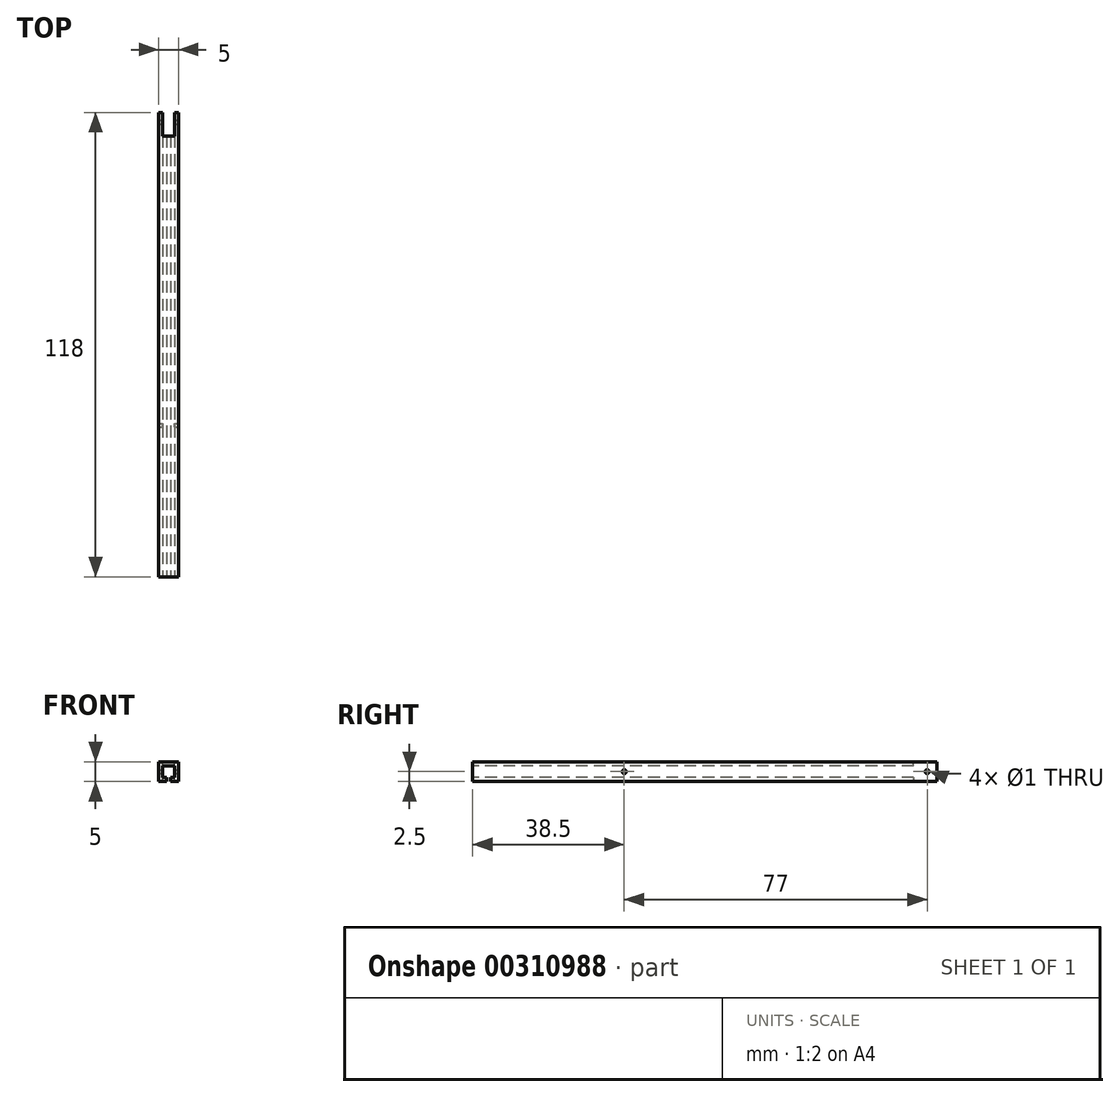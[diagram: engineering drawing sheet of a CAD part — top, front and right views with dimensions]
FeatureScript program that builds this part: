
annotation { "Feature Type Name" : "Feature", "Feature Type Description" : "" }
export const myFeature = defineFeature(function(context is Context, id is Id, definition is map)
    precondition{}
    {
        {
            var Q0;
            Q0=qCreatedBy(makeId("Front.planeOp"),FACE);
            var sketch = newSketch(context, id + "F0", { "sketchPlane" : qUnion([Q0])});
            skLineSegment(sketch, "E0.bottom", {"start": v(2.5, -2.5) * mm, "end": v(-2.5, -2.5) * mm});
            skLineSegment(sketch, "E0.top", {"start": v(2.5, 2.5) * mm, "end": v(-2.5, 2.5) * mm});
            skLineSegment(sketch, "E0.left", {"start": v(2.5, -2.5) * mm, "end": v(2.5, 2.5) * mm});
            skLineSegment(sketch, "E0.right", {"start": v(-2.5, -2.5) * mm, "end": v(-2.5, 2.5) * mm});
            skPoint(sketch, "E0.middle", {"position": v(0, 0) * mm});
            skSolve(sketch);
        }
        {
            var Q0;
            Q0=makeQuery(id+"F0.imprint","IMPRINT",FACE,{"disambiguationData":[TD([[makeQuery(id+"F0.imprint","IMPRINT",EDGE,{"derivedFrom":sQuery(id+"F0.wireOp",EDGE,"E0.bottom")}),-1.0]])]});
            extrude(context, id + "F1", {"entities" : qUnion([Q0]), "depth" : 118 * mm});
        }
        {
            var Q0;
            Q0=makeQuery(id+"F1.opExtrude","CAP_FACE",FACE,{"disambiguationData":[OSD([sQuery(id+"F0.wireOp",EDGE,"E0.bottom"),sQuery(id+"F0.wireOp",EDGE,"E0.top"),sQuery(id+"F0.wireOp",EDGE,"E0.left"),sQuery(id+"F0.wireOp",EDGE,"E0.right")])],"isStart":false});
            var sketch = newSketch(context, id + "F2", { "sketchPlane" : qUnion([Q0])});
            skLineSegment(sketch, "E1.bottom", {"start": v(1.5, -1.5) * mm, "end": v(-1.5, -1.5) * mm});
            skLineSegment(sketch, "E1.top", {"start": v(1.5, 1.5) * mm, "end": v(-1.5, 1.5) * mm});
            skLineSegment(sketch, "E1.left", {"start": v(1.5, -1.5) * mm, "end": v(1.5, 1.5) * mm});
            skLineSegment(sketch, "E1.right", {"start": v(-1.5, -1.5) * mm, "end": v(-1.5, 1.5) * mm});
            skPoint(sketch, "E1.middle", {"position": v(0, 0) * mm});
            skLineSegment(sketch, "E2", {"start": v(-0.5, -1.5) * mm, "end": v(-0.5, -2.5) * mm});
            skLineSegment(sketch, "E3", {"start": v(0.5, -1.5) * mm, "end": v(0.5, -2.5) * mm});
            skSolve(sketch);
        }
        {
            var Q0;
            Q0=makeQuery(id+"F2.imprint","IMPRINT",FACE,{"disambiguationData":[TD([[makeQuery(id+"F2.imprint","IMPRINT",EDGE,{"derivedFrom":sQuery(id+"F2.wireOp",EDGE,"E1.top")}),1.0]])]});
            var Q1;
            {var subQ0=sQuery(id+"F2.wireOp",EDGE,"E2");Q1=makeQuery(id+"F2.imprint","IMPRINT",FACE,{"disambiguationData":[TD([[makeQuery(id+"F2.imprint","IMPRINT",EDGE,{"derivedFrom":subQ0}),1.0]])]});}
            extrude(context, id + "F3", {"entities" : qUnion([Q0, Q1]), "operationType" : NewBodyOperationType.REMOVE, "endBound" : BoundingType.THROUGH_ALL, "oppositeDirection" : true, "depth" : 25 * mm});
        }
        {
            var Q0;
            Q0=makeQuery(id+"F1.opExtrude","SWEPT_FACE",FACE,{"disambiguationData":[OSD([sQuery(id+"F0.wireOp",EDGE,"E0.left")])]});
            var sketch = newSketch(context, id + "F4", { "sketchPlane" : qUnion([Q0])});
            skCircle(sketch, "E4", {"center": v(-79.5, 0) * mm, "radius": 0.5 * mm});
            skPoint(sketch, "E4.centerSnap0", {"position": v(-118, 0) * mm});
            skSolve(sketch);
        }
        {
            var Q0;
            Q0=makeQuery(id+"F4.imprint","IMPRINT",FACE,{"disambiguationData":[TD([[makeQuery(id+"F4.imprint","IMPRINT",EDGE,{"derivedFrom":sQuery(id+"F4.wireOp",EDGE,"E4")}),1.0]])]});
            extrude(context, id + "F5", {"entities" : qUnion([Q0]), "operationType" : NewBodyOperationType.REMOVE, "endBound" : BoundingType.THROUGH_ALL, "oppositeDirection" : true, "depth" : 25 * mm});
        }
        {
            var Q0;
            Q0=makeQuery(id+"F1.opExtrude","SWEPT_FACE",FACE,{"disambiguationData":[OSD([sQuery(id+"F0.wireOp",EDGE,"E0.left")])]});
            var sketch = newSketch(context, id + "F6", { "sketchPlane" : qUnion([Q0])});
            skCircle(sketch, "E5", {"center": v(-2.5, 0) * mm, "radius": 0.5 * mm});
            skSolve(sketch);
        }
        {
            var Q0;
            Q0=makeQuery(id+"F6.imprint","IMPRINT",FACE,{"disambiguationData":[TD([[makeQuery(id+"F6.imprint","IMPRINT",EDGE,{"derivedFrom":sQuery(id+"F6.wireOp",EDGE,"E5")}),1.0]])]});
            extrude(context, id + "F7", {"entities" : qUnion([Q0]), "operationType" : NewBodyOperationType.REMOVE, "endBound" : BoundingType.THROUGH_ALL, "oppositeDirection" : true, "depth" : 25 * mm});
        }
        {
            var Q0;
            Q0=makeQuery(id+"F1.opExtrude","SWEPT_FACE",FACE,{"disambiguationData":[OSD([sQuery(id+"F0.wireOp",EDGE,"E0.top")])]});
            var sketch = newSketch(context, id + "F8", { "sketchPlane" : qUnion([Q0])});
            skLineSegment(sketch, "E6.bottom", {"start": v(1.5, 0) * mm, "end": v(-1.5, 0) * mm});
            skLineSegment(sketch, "E6.top", {"start": v(1.5, -6) * mm, "end": v(-1.5, -6) * mm});
            skLineSegment(sketch, "E6.left", {"start": v(1.5, 0) * mm, "end": v(1.5, -6) * mm});
            skLineSegment(sketch, "E6.right", {"start": v(-1.5, 0) * mm, "end": v(-1.5, -6) * mm});
            skSolve(sketch);
        }
        {
            var Q0;
            Q0=makeQuery(id+"F8.imprint","IMPRINT",FACE,{"disambiguationData":[TD([[makeQuery(id+"F8.imprint","IMPRINT",EDGE,{"derivedFrom":sQuery(id+"F8.wireOp",EDGE,"E6.bottom")}),1.0]])]});
            extrude(context, id + "F9", {"entities" : qUnion([Q0]), "operationType" : NewBodyOperationType.REMOVE, "endBound" : BoundingType.THROUGH_ALL, "oppositeDirection" : true, "depth" : 25 * mm});
        }
    });
